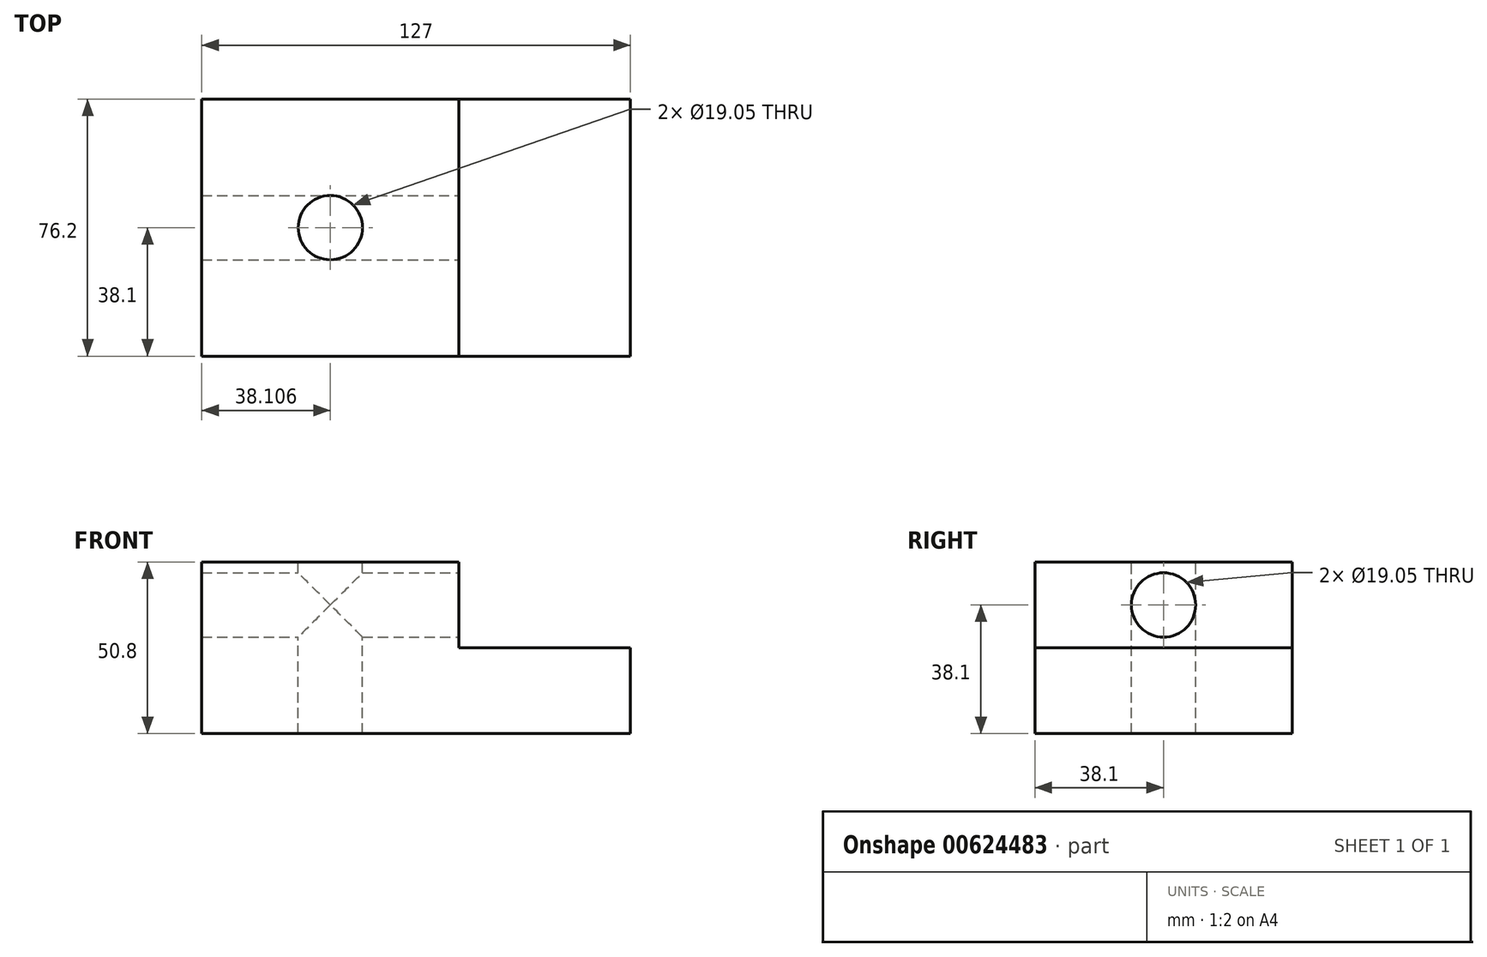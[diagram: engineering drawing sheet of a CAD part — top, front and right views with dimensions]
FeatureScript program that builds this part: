
annotation { "Feature Type Name" : "Feature", "Feature Type Description" : "" }
export const myFeature = defineFeature(function(context is Context, id is Id, definition is map)
    precondition{}
    {
        {
            var Q0;
            Q0=qCreatedBy(makeId("Front.planeOp"),FACE);
            var sketch = newSketch(context, id + "F0", { "sketchPlane" : qUnion([Q0])});
            skLineSegment(sketch, "E0.bottom", {"start": v(-53.74, 0) * mm, "end": v(73.26, 0) * mm});
            skLineSegment(sketch, "E0.top", {"start": v(-53.74, 50.8) * mm, "end": v(73.26, 50.8) * mm});
            skLineSegment(sketch, "E0.left", {"start": v(-53.74, 0) * mm, "end": v(-53.74, 50.8) * mm});
            skLineSegment(sketch, "E0.right", {"start": v(73.26, 0) * mm, "end": v(73.26, 50.8) * mm});
            skLineSegment(sketch, "E1", {"start": v(73.26, 25.4) * mm, "end": v(22.47, 25.4) * mm});
            skLineSegment(sketch, "E2", {"start": v(22.47, 25.4) * mm, "end": v(22.47, 50.8) * mm});
            skSolve(sketch);
        }
        {
            var Q0;
            {var subQ1=sQuery(id+"F0.wireOp",EDGE,"E0.bottom");Q0=makeQuery(id+"F0.imprint","IMPRINT",FACE,{"disambiguationData":[TD([[makeQuery(id+"F0.imprint","IMPRINT",EDGE,{"derivedFrom":subQ1}),1.0]])]});}
            extrude(context, id + "F1", {"entities" : qUnion([Q0]), "endBound" : BoundingType.SYMMETRIC, "depth" : 76.2 * mm, "offsetDistance" : 25.4 * mm});
        }
        {
            var Q0;
            Q0=makeQuery(id+"F1.opExtrude","SWEPT_FACE",FACE,{"disambiguationData":[OSD([sQuery(id+"F0.wireOp",EDGE,"E2")])]});
            var sketch = newSketch(context, id + "F2", { "sketchPlane" : qUnion([Q0])});
            skPoint(sketch, "E3", {"position": v(0, 38.1) * mm});
            skPoint(sketch, "E3.positionSnap0", {"position": v(38.1, 38.1) * mm});
            skPoint(sketch, "E3.positionSnap1", {"position": v(0, 50.8) * mm});
            skSolve(sketch);
        }
        {
            var Q0;
            Q0=sQuery(id+"F2.wireOp",VERTEX,"E3");
            var Q1;
            Q1=makeQuery(id+"F1.opExtrude","SWEPT_BODY",BODY,{"disambiguationData":[OSD([sQuery(id+"F0.wireOp",EDGE,"E0.bottom"),sQuery(id+"F0.wireOp",EDGE,"E0.top"),sQuery(id+"F0.wireOp",EDGE,"E0.left"),sQuery(id+"F0.wireOp",EDGE,"E0.right"),sQuery(id+"F0.wireOp",EDGE,"E1"),sQuery(id+"F0.wireOp",EDGE,"E2")])]});
            hole(context, id + "F3", {"style" : HoleStyle.SIMPLE, "endStyle" : HoleEndStyle.THROUGH, "holeDiameter" : 19.05 * mm, "majorDiameter" : 6.35 * mm, "isTappedThrough" : true, "tappedDepth" : 12.7 * mm, "tapClearance" : 3, "locations" : qUnion([Q0]), "scope" : qUnion([Q1])});
        }
        {
            var Q0;
            Q0=makeQuery(id+"F1.opExtrude","SWEPT_FACE",FACE,{"disambiguationData":[OSD([sQuery(id+"F0.wireOp",EDGE,"E0.top")])]});
            var sketch = newSketch(context, id + "F4", { "sketchPlane" : qUnion([Q0])});
            skPoint(sketch, "E4", {"position": v(-15.63, 0) * mm});
            skPoint(sketch, "E4.positionSnap0", {"position": v(-15.63, 38.1) * mm});
            skPoint(sketch, "E4.positionSnap1", {"position": v(-53.74, 0) * mm});
            skSolve(sketch);
        }
        {
            var Q0;
            Q0=sQuery(id+"F4.wireOp",VERTEX,"E4");
            var Q1;
            Q1=makeQuery(id+"F1.opExtrude","SWEPT_BODY",BODY,{"disambiguationData":[OSD([sQuery(id+"F0.wireOp",EDGE,"E0.bottom"),sQuery(id+"F0.wireOp",EDGE,"E0.top"),sQuery(id+"F0.wireOp",EDGE,"E0.left"),sQuery(id+"F0.wireOp",EDGE,"E0.right"),sQuery(id+"F0.wireOp",EDGE,"E1"),sQuery(id+"F0.wireOp",EDGE,"E2")])]});
            hole(context, id + "F5", {"style" : HoleStyle.SIMPLE, "endStyle" : HoleEndStyle.THROUGH, "holeDiameter" : 19.05 * mm, "majorDiameter" : 6.35 * mm, "isTappedThrough" : true, "tappedDepth" : 12.7 * mm, "tapClearance" : 3, "locations" : qUnion([Q0]), "scope" : qUnion([Q1])});
        }
    });
